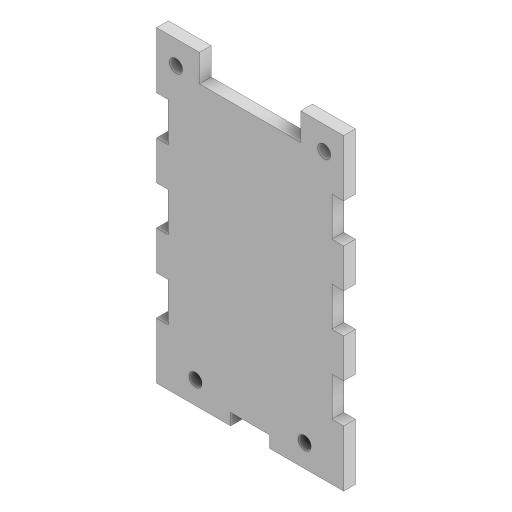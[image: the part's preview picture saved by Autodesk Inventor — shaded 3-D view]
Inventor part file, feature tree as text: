
AUTODESK INVENTOR PART (.ipt)
format: ipt  version: 2023.3 (Build 273359000, 359)  size: 167,936 bytes
history: native  units: mm
features: extrude x1, sketch x1
ambient origin geometry x8: Origin, YZ Plane, XZ Plane, XY Plane, X Axis, Y Axis, Z Axis, Center Point
bodies: Solid1 (feature_tree)
feature tree (2):
  extrude  "Extrusion1"  Depth=3.0mm TaperAngle=0.0deg
  sketch  "Sketch1"  dims[d1=20.0mm d3=10.0mm d5=20.0mm d7=10.0mm d9=20.0mm d11=10.0mm d13=20.0mm d15=10.0mm d16=3.3mm d17=3.3mm d18=28.0mm d19=14.0mm d20=3.3mm d21=3.3mm d22=38.0mm d23=19.0mm d24=34.0mm d25=44.0mm d26=3.25mm d27=20.0mm d28=5.0mm d29=10.0mm d30=9.0mm d31=26.0mm d32=7.0mm d33=1.0mm d34=3.0mm d35=10.0mm d36=10.0mm d37=3.0mm d38=10.0mm d39=3.0mm d40=20.0mm d41=20.0mm d42=3.0mm d43=10.0mm d44=20.0mm d45=20.0mm d46=10.0mm d47=10.0mm d48=10.0mm d49=10.0mm d50=3.0mm d51=0.0mm d52=26.0mm d53=7.0mm]
